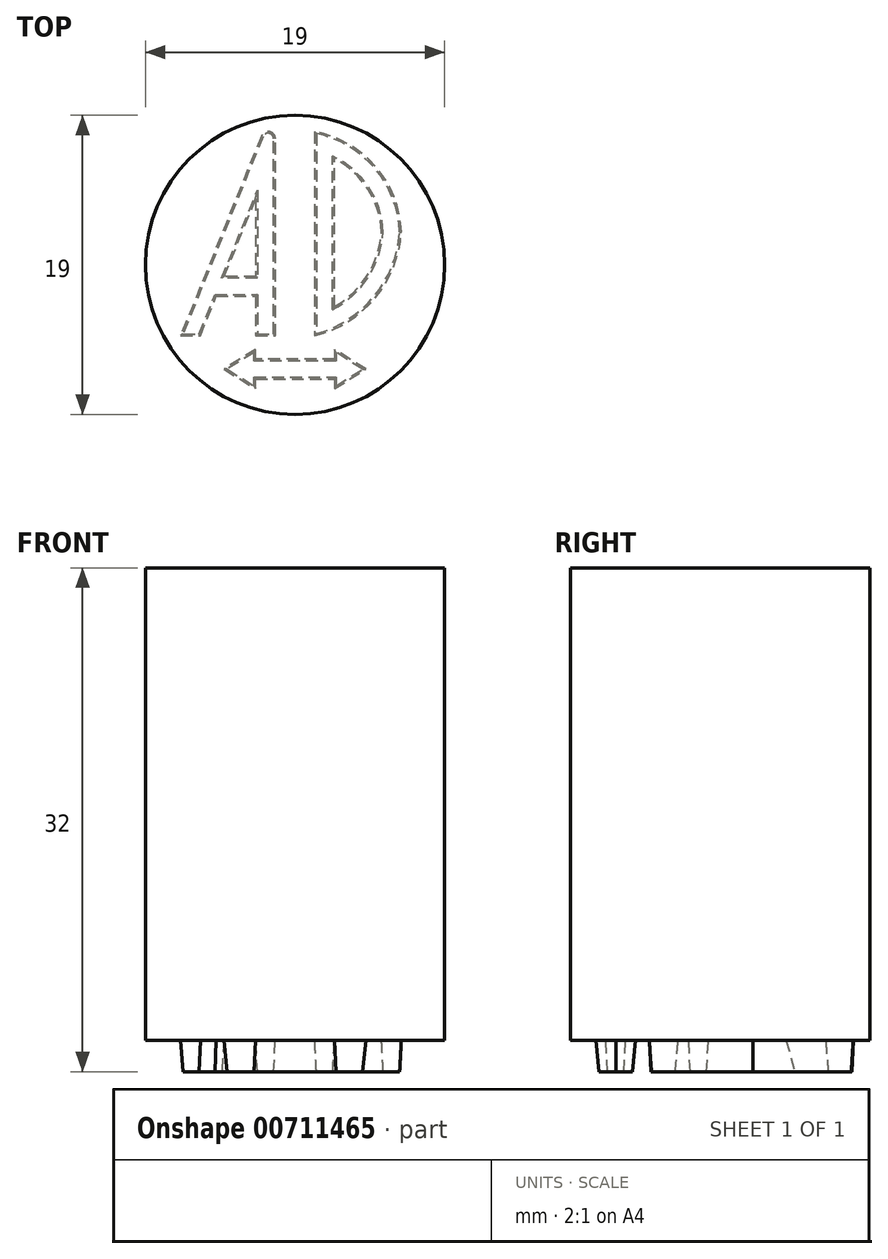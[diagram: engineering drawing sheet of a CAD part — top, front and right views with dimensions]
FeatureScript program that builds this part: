
annotation { "Feature Type Name" : "Feature", "Feature Type Description" : "" }
export const myFeature = defineFeature(function(context is Context, id is Id, definition is map)
    precondition{}
    {
        {
            var Q0;
            Q0=qCreatedBy(makeId("Top.planeOp"),FACE);
            var sketch = newSketch(context, id + "F0", { "sketchPlane" : qUnion([Q0])});
            skCircle(sketch, "E0", {"center": v(0, 0) * mm, "radius": 9.5 * mm});
            skLineSegment(sketch, "E1", {"start": v(-1.25, -4.5) * mm, "end": v(-1.25, 8) * mm});
            skLineSegment(sketch, "E2", {"start": v(-2.14, 8.17) * mm, "end": v(-7.26, -4.5) * mm});
            skLineSegment(sketch, "E3", {"start": v(-7.26, -4.5) * mm, "end": v(-6.01, -4.5) * mm});
            skLineSegment(sketch, "E4", {"start": v(-6.01, -4.5) * mm, "end": v(-5, -2) * mm});
            skLineSegment(sketch, "E5", {"start": v(-5, -2) * mm, "end": v(-2.5, -2) * mm});
            skLineSegment(sketch, "E6", {"start": v(-2.5, -2) * mm, "end": v(-2.5, -4.5) * mm});
            skLineSegment(sketch, "E7", {"start": v(-2.5, -4.5) * mm, "end": v(-1.25, -4.5) * mm});
            skLineSegment(sketch, "E8", {"start": v(-4.5, -0.75) * mm, "end": v(-2.5, 4.2) * mm});
            skLineSegment(sketch, "E9", {"start": v(-2.5, -0.75) * mm, "end": v(-2.5, 4.2) * mm});
            skLineSegment(sketch, "E10", {"start": v(-4.5, -0.75) * mm, "end": v(-2.5, -0.75) * mm});
            skPoint(sketch, "E11.visualSharp", {"position": v(-1.25, 10.38) * mm});
            skArc(sketch, "E11.filletArc", {"start": v(-1.25, 8) * mm, "mid": v(-1.62, 8.45) * mm, "end": v(-2.14, 8.17) * mm});
            skLineSegment(sketch, "E12", {"start": v(1.25, -4.5) * mm, "end": v(1.25, 8.45) * mm});
            skPoint(sketch, "E12.endSnap0", {"position": v(-1.62, 8.45) * mm});
            skArc(sketch, "E13", {"start": v(6.75, 2.07) * mm, "mid": v(5.12, 6.23) * mm, "end": v(1.25, 8.45) * mm});
            skArc(sketch, "E14", {"start": v(1.25, -4.5) * mm, "mid": v(5.08, -2.11) * mm, "end": v(6.75, 2.07) * mm});
            skLineSegment(sketch, "E15", {"start": v(-2.5, -6) * mm, "end": v(2.5, -6) * mm});
            skLineSegment(sketch, "E16", {"start": v(2.5, -6) * mm, "end": v(2.5, -5.38) * mm});
            skLineSegment(sketch, "E17", {"start": v(2.5, -5.38) * mm, "end": v(4.5, -6.63) * mm});
            skLineSegment(sketch, "E18", {"start": v(4.5, -6.62) * mm, "end": v(2.5, -7.88) * mm});
            skLineSegment(sketch, "E19", {"start": v(2.5, -7.88) * mm, "end": v(2.5, -7.25) * mm});
            skLineSegment(sketch, "E20", {"start": v(2.5, -7.25) * mm, "end": v(-2.5, -7.25) * mm});
            skLineSegment(sketch, "E21", {"start": v(-2.5, -7.25) * mm, "end": v(-2.5, -7.88) * mm});
            skLineSegment(sketch, "E22", {"start": v(-2.5, -7.88) * mm, "end": v(-4.5, -6.62) * mm});
            skLineSegment(sketch, "E23", {"start": v(-4.5, -6.63) * mm, "end": v(-2.5, -5.38) * mm});
            skLineSegment(sketch, "E24", {"start": v(-2.5, -5.38) * mm, "end": v(-2.5, -6) * mm});
            skArc(sketch, "E25.0", {"start": v(5.5, 2.09) * mm, "mid": v(4.63, 4.81) * mm, "end": v(2.5, 6.73) * mm});
            skArc(sketch, "E25.1", {"start": v(2.5, -2.67) * mm, "mid": v(4.6, -0.66) * mm, "end": v(5.5, 2.09) * mm});
            skLineSegment(sketch, "E25.2", {"start": v(2.5, -2.67) * mm, "end": v(2.5, 6.73) * mm});
            skSolve(sketch);
        }
        {
            var Q0;
            Q0=makeQuery(id+"F0.imprint","IMPRINT",FACE,{"disambiguationData":[TD([[makeQuery(id+"F0.imprint","IMPRINT",EDGE,{"derivedFrom":sQuery(id+"F0.wireOp",EDGE,"E1")}),1.0]])]});
            var Q1;
            Q1=makeQuery(id+"F0.imprint","IMPRINT",FACE,{"disambiguationData":[TD([[makeQuery(id+"F0.imprint","IMPRINT",EDGE,{"derivedFrom":sQuery(id+"F0.wireOp",EDGE,"E12")}),-1.0]])]});
            var Q2;
            Q2=makeQuery(id+"F0.imprint","IMPRINT",FACE,{"disambiguationData":[TD([[makeQuery(id+"F0.imprint","IMPRINT",EDGE,{"derivedFrom":sQuery(id+"F0.wireOp",EDGE,"E15")}),-1.0]])]});
            extrude(context, id + "F1", {"entities" : qUnion([Q0, Q1, Q2]), "oppositeDirection" : true, "depth" : 2 * mm, "offsetDistance" : 25 * mm, "hasDraft" : true, "draftAngle" : 3 * degree, "draftPullDirection" : true});
        }
        {
            var Q0;
            Q0=makeQuery(id+"F0.imprint","IMPRINT",FACE,{"disambiguationData":[TD([[makeQuery(id+"F0.imprint","IMPRINT",EDGE,{"derivedFrom":sQuery(id+"F0.wireOp",EDGE,"E25.0")}),1.0]])]});
            var Q1;
            Q1=makeQuery(id+"F0.imprint","IMPRINT",FACE,{"disambiguationData":[TD([[makeQuery(id+"F0.imprint","IMPRINT",EDGE,{"derivedFrom":sQuery(id+"F0.wireOp",EDGE,"E12")}),-1.0]])]});
            var Q2;
            Q2=makeQuery(id+"F0.imprint","IMPRINT",FACE,{"disambiguationData":[TD([[makeQuery(id+"F0.imprint","IMPRINT",EDGE,{"derivedFrom":sQuery(id+"F0.wireOp",EDGE,"E0")}),1.0]])]});
            var Q3;
            Q3=makeQuery(id+"F0.imprint","IMPRINT",FACE,{"disambiguationData":[TD([[makeQuery(id+"F0.imprint","IMPRINT",EDGE,{"derivedFrom":sQuery(id+"F0.wireOp",EDGE,"E15")}),-1.0]])]});
            var Q4;
            Q4=makeQuery(id+"F0.imprint","IMPRINT",FACE,{"disambiguationData":[TD([[makeQuery(id+"F0.imprint","IMPRINT",EDGE,{"derivedFrom":sQuery(id+"F0.wireOp",EDGE,"E1")}),1.0]])]});
            var Q5;
            Q5=makeQuery(id+"F0.imprint","IMPRINT",FACE,{"disambiguationData":[TD([[makeQuery(id+"F0.imprint","IMPRINT",EDGE,{"derivedFrom":sQuery(id+"F0.wireOp",EDGE,"E8")}),-1.0]])]});
            extrude(context, id + "F2", {"entities" : qUnion([Q0, Q1, Q2, Q3, Q4, Q5]), "depth" : 30 * mm, "offsetDistance" : 25 * mm});
        }
    });
